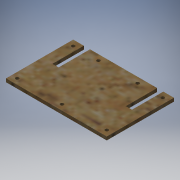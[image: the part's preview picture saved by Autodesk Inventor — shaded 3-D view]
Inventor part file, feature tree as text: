
AUTODESK INVENTOR PART (.ipt)
format: ipt  version: 2018 (Build 220112000, 112)  size: 152,064 bytes
history: native  units: mm
features: extrude x1
ambient origin geometry x8: Origin, YZ Plane, XZ Plane, XY Plane, X Axis, Y Axis, Z Axis, Center Point
bodies: Body1 (feature_tree)
feature tree (1):
  extrude  "Extrusion3"  Depth=140.0mm
